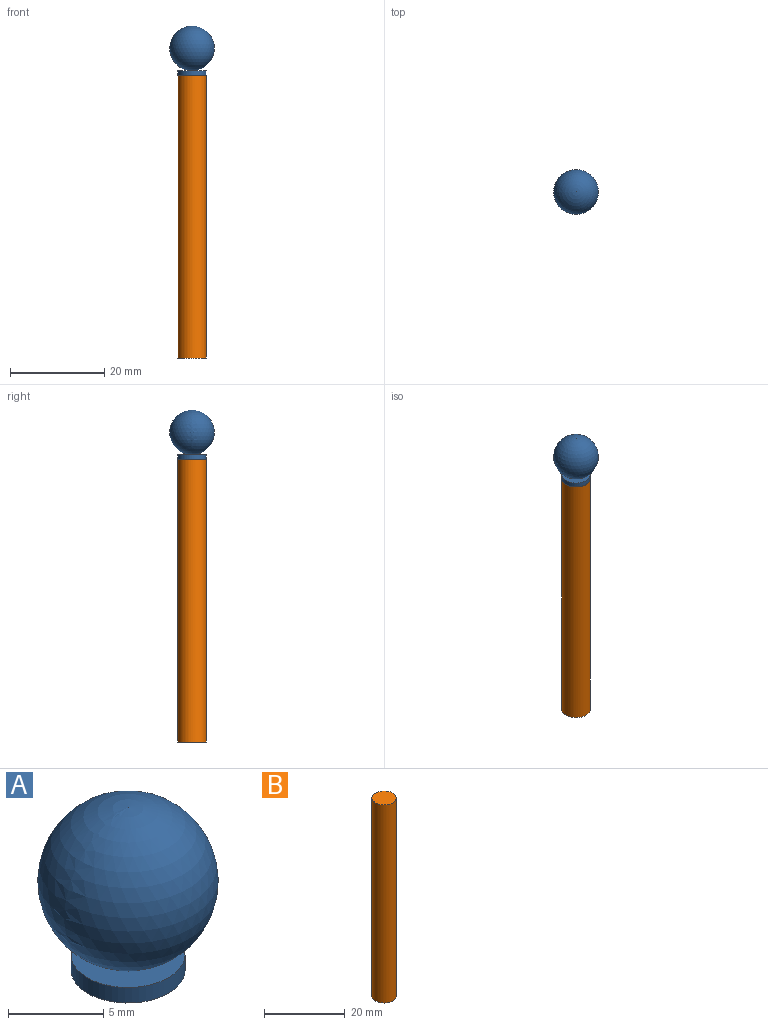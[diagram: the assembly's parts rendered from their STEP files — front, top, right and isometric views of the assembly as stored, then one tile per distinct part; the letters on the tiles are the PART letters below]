
ASSEMBLY  parts=2 mates=1
PART A: 5 faces, bbox 9.5x9.5x10.5 mm
  f0: sphere r=4.75mm, area 280.4mm2, adj f1
  f1: cylinder r=1mm len=2mm, axis (0,0,-1), area 0.7mm2, adj f0,f2
  f2: plane 6x6mm, normal (0,0,1), area 25.1mm2, adj f1,f3
  f3: cylinder r=3mm len=6mm, axis (0,0,-1), area 18.8mm2, adj f2,f4
  f4: plane 6x6mm, normal (0,0,-1), area 28.3mm2, adj f3
PART B: 3 faces, bbox 6x6x60 mm
  f0: cylinder r=3mm len=60mm, axis (0,0,-1), area 1131mm2, adj f1,f2
  f1: plane 6x6mm, normal (0,0,1), area 28.3mm2, adj f0
  f2: plane 6x6mm, normal (0,0,-1), area 28.3mm2, adj f0
PLACE A t=(-20.99,16.96,35.77)mm
PLACE B t=(-17.99,16.96,-24.23)mm
MATE slider B.f0 <-> A.f1  axis (0,0,1) through (-17.99,16.96,35.77)mm
